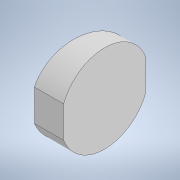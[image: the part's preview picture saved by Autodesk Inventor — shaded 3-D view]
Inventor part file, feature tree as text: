
AUTODESK INVENTOR PART (.ipt)
format: ipt  version: 2022 (Build 260153000, 153)  size: 128,512 bytes
history: native  units: mm
features: sketch x4, extrude x3, other x2, revolve x1, projected_geometry x1
ambient origin geometry x8: Origin, YZ Plane, XZ Plane, XY Plane, X Axis, Y Axis, Z Axis, Center Point
bodies: Body1 (feature_tree)
feature tree (11):
  other  "Твердое тело1"
  revolve  "Вращение1"
  extrude  "Выдавливание1"  Depth=20.0mm
  extrude  "Выдавливание2"  Depth=30.0mm
  other  "РабПлоскость1"
  extrude  "Выдавливание3"  TaperAngle=90.0deg  [1 undecoded]
  sketch  "Эскиз1"
  sketch  "Эскиз2"
  sketch  "Эскиз3"
  sketch  "Эскиз4"
  projected_geometry  "Спроецированная петля1"
note: 1 required parameter value undecoded (feature->parameter linkage not recoverable at this tier; creation-order binding heuristic only, values carry confidence <= 0.55)
